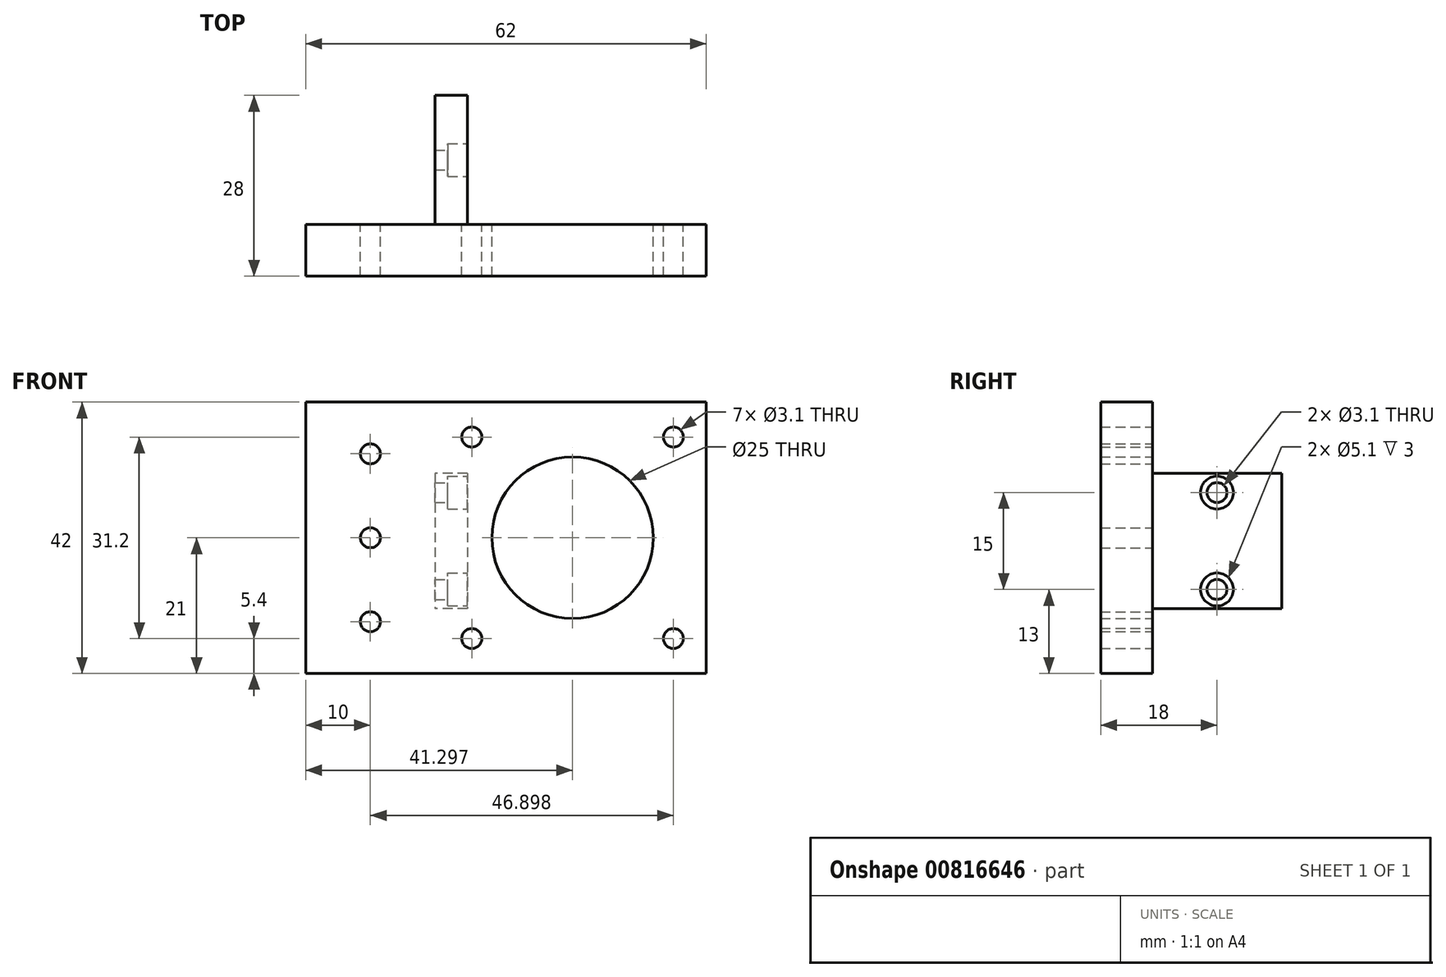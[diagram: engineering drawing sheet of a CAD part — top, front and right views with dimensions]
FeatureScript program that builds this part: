
annotation { "Feature Type Name" : "Feature", "Feature Type Description" : "" }
export const myFeature = defineFeature(function(context is Context, id is Id, definition is map)
    precondition{}
    {
        {
            var Q0;
            Q0=qCreatedBy(makeId("Front.planeOp"),FACE);
            var sketch = newSketch(context, id + "F0", { "sketchPlane" : qUnion([Q0])});
            skLineSegment(sketch, "E0.bottom", {"start": v(0, 0) * mm, "end": v(62, 0) * mm});
            skLineSegment(sketch, "E0.top", {"start": v(0, 42) * mm, "end": v(62, 42) * mm});
            skLineSegment(sketch, "E0.left", {"start": v(0, 0) * mm, "end": v(0, 42) * mm});
            skLineSegment(sketch, "E0.right", {"start": v(62, 0) * mm, "end": v(62, 42) * mm});
            skCircle(sketch, "E1", {"center": v(41.3, 21) * mm, "radius": 12.5 * mm});
            skCircle(sketch, "E2", {"center": v(10, 34) * mm, "radius": 1.55 * mm});
            skCircle(sketch, "E3", {"center": v(10, 21) * mm, "radius": 1.55 * mm});
            skCircle(sketch, "E4", {"center": v(10, 8) * mm, "radius": 1.55 * mm});
            skCircle(sketch, "E5", {"center": v(25.7, 36.6) * mm, "radius": 1.55 * mm});
            skCircle(sketch, "E6", {"center": v(25.7, 5.4) * mm, "radius": 1.55 * mm});
            skCircle(sketch, "E7", {"center": v(56.9, 36.6) * mm, "radius": 1.55 * mm});
            skCircle(sketch, "E8", {"center": v(56.9, 5.4) * mm, "radius": 1.55 * mm});
            skSolve(sketch);
        }
        {
            var Q0;
            Q0 = qSketchRegion(id + "F0", true);
            extrude(context, id + "F1", {"entities" : qUnion([Q0]), "depth" : 8 * mm, "offsetDistance" : 25 * mm});
        }
        {
            var Q0;
            Q0=makeQuery(id+"F1.opExtrude","CAP_FACE",FACE,{"disambiguationData":[OSD([sQuery(id+"F0.wireOp",EDGE,"E0.bottom"),sQuery(id+"F0.wireOp",EDGE,"E0.top"),sQuery(id+"F0.wireOp",EDGE,"E0.left"),sQuery(id+"F0.wireOp",EDGE,"E0.right"),sQuery(id+"F0.wireOp",EDGE,"E1"),sQuery(id+"F0.wireOp",EDGE,"E2"),sQuery(id+"F0.wireOp",EDGE,"E3"),sQuery(id+"F0.wireOp",EDGE,"E4"),sQuery(id+"F0.wireOp",EDGE,"E5"),sQuery(id+"F0.wireOp",EDGE,"E6"),sQuery(id+"F0.wireOp",EDGE,"E7"),sQuery(id+"F0.wireOp",EDGE,"E8")])],"isStart":true});
            var sketch = newSketch(context, id + "F2", { "sketchPlane" : qUnion([Q0])});
            skLineSegment(sketch, "E9.bottom", {"start": v(-25, 31) * mm, "end": v(-20, 31) * mm});
            skLineSegment(sketch, "E9.top", {"start": v(-25, 10) * mm, "end": v(-20, 10) * mm});
            skLineSegment(sketch, "E9.left", {"start": v(-25, 31) * mm, "end": v(-25, 10) * mm});
            skLineSegment(sketch, "E9.right", {"start": v(-20, 31) * mm, "end": v(-20, 10) * mm});
            skSolve(sketch);
        }
        {
            var Q0;
            Q0 = qSketchRegion(id + "F2", true);
            extrude(context, id + "F3", {"entities" : qUnion([Q0]), "operationType" : NewBodyOperationType.ADD, "depth" : 20 * mm, "offsetDistance" : 25 * mm});
        }
        {
            var Q0;
            Q0=makeQuery(id+"F3.opExtrude","SWEPT_FACE",FACE,{"disambiguationData":[OSD([sQuery(id+"F2.wireOp",EDGE,"E9.left")])]});
            var sketch = newSketch(context, id + "F4", { "sketchPlane" : qUnion([Q0])});
            skCircle(sketch, "E10", {"center": v(10, 28) * mm, "radius": 1.55 * mm});
            skPoint(sketch, "E10.centerSnap0", {"position": v(10, 31) * mm});
            skCircle(sketch, "E11", {"center": v(10, 13) * mm, "radius": 1.55 * mm});
            skSolve(sketch);
        }
        {
            var Q0;
            Q0 = qSketchRegion(id + "F4", true);
            extrude(context, id + "F5", {"entities" : qUnion([Q0]), "operationType" : NewBodyOperationType.REMOVE, "oppositeDirection" : true, "depth" : 25 * mm, "offsetDistance" : 25 * mm});
        }
        {
            var Q0;
            Q0=makeQuery(id+"F3.opExtrude","SWEPT_FACE",FACE,{"disambiguationData":[OSD([sQuery(id+"F2.wireOp",EDGE,"E9.left")])]});
            var sketch = newSketch(context, id + "F6", { "sketchPlane" : qUnion([Q0])});
            skCircle(sketch, "E12", {"center": v(10, 28) * mm, "radius": 2.55 * mm});
            skCircle(sketch, "E13", {"center": v(10, 13) * mm, "radius": 2.55 * mm});
            skSolve(sketch);
        }
        {
            var Q0;
            Q0 = qSketchRegion(id + "F6", true);
            extrude(context, id + "F7", {"entities" : qUnion([Q0]), "operationType" : NewBodyOperationType.REMOVE, "oppositeDirection" : true, "depth" : 3 * mm, "offsetDistance" : 25 * mm});
        }
    });
